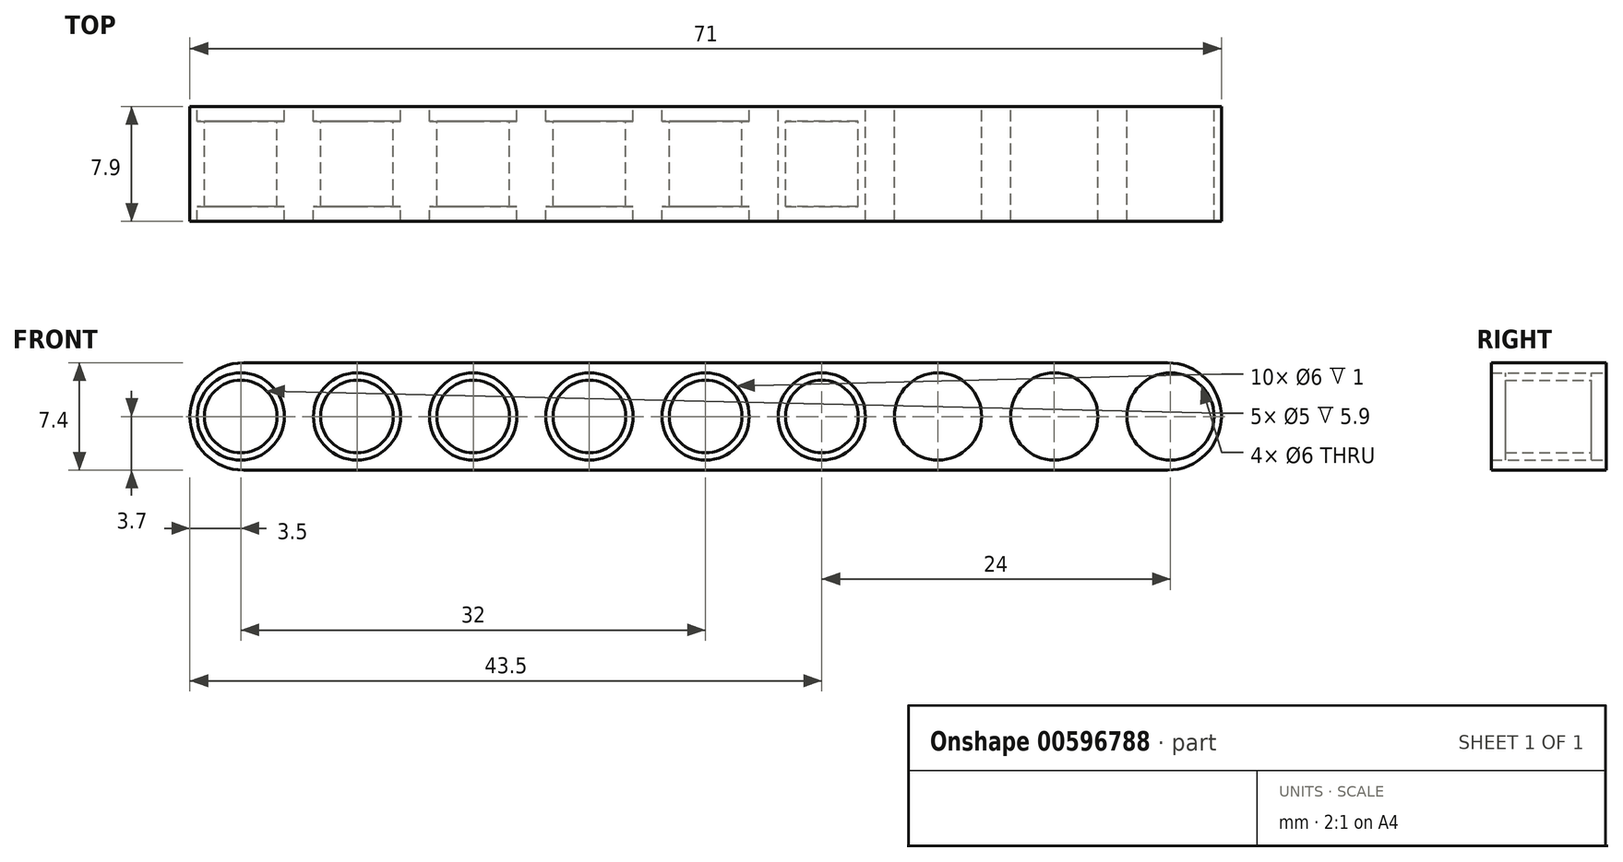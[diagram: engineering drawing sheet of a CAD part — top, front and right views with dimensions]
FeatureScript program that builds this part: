
annotation { "Feature Type Name" : "Feature", "Feature Type Description" : "" }
export const myFeature = defineFeature(function(context is Context, id is Id, definition is map)
    precondition{}
    {
        {
            var Q0;
            Q0=qCreatedBy(makeId("Front.planeOp"),FACE);
            var sketch = newSketch(context, id + "F0", { "sketchPlane" : qUnion([Q0])});
            skLineSegment(sketch, "E0.bottom", {"start": v(35.5, 3.7) * mm, "end": v(-35.5, 3.7) * mm});
            skLineSegment(sketch, "E0.top", {"start": v(35.5, -3.7) * mm, "end": v(-35.5, -3.7) * mm});
            skLineSegment(sketch, "E0.left", {"start": v(35.5, 3.7) * mm, "end": v(35.5, -3.7) * mm});
            skLineSegment(sketch, "E0.right", {"start": v(-35.5, 3.7) * mm, "end": v(-35.5, -3.7) * mm});
            skPoint(sketch, "E0.middle", {"position": v(0, 0) * mm});
            skCircle(sketch, "E1", {"center": v(0, 0) * mm, "radius": 2.5 * mm});
            skCircle(sketch, "E2", {"center": v(-8, 0) * mm, "radius": 2.5 * mm});
            skCircle(sketch, "E3", {"center": v(-16, 0) * mm, "radius": 2.5 * mm});
            skCircle(sketch, "E4", {"center": v(-24, 0) * mm, "radius": 2.5 * mm});
            skCircle(sketch, "E5", {"center": v(-32, 0) * mm, "radius": 2.5 * mm});
            skCircle(sketch, "E6", {"center": v(0, 0) * mm, "radius": 3 * mm});
            skCircle(sketch, "E7", {"center": v(-8, 0) * mm, "radius": 3 * mm});
            skCircle(sketch, "E8", {"center": v(-16, 0) * mm, "radius": 3 * mm});
            skCircle(sketch, "E9", {"center": v(-24, 0) * mm, "radius": 3 * mm});
            skCircle(sketch, "E10", {"center": v(-32, 0) * mm, "radius": 3 * mm});
            skLineSegment(sketch, "E11", {"start": v(0, 8.17) * mm, "end": v(0, -9.62) * mm, "construction": true});
            skPoint(sketch, "E11.endSnap0", {"position": v(0, -3.7) * mm});
            skCircle(sketch, "E12.MirrorC", {"center": v(8, 0) * mm, "radius": 2.5 * mm});
            skCircle(sketch, "E13.MirrorC", {"center": v(8, 0) * mm, "radius": 3 * mm});
            skCircle(sketch, "E14.MirrorC", {"center": v(16, 0) * mm, "radius": 3 * mm});
            skCircle(sketch, "E15.MirrorC", {"center": v(16, 0) * mm, "radius": 2.5 * mm});
            skCircle(sketch, "E16.MirrorC", {"center": v(24, 0) * mm, "radius": 3 * mm});
            skCircle(sketch, "E17.MirrorC", {"center": v(24, 0) * mm, "radius": 2.5 * mm});
            skCircle(sketch, "E18.MirrorC", {"center": v(32, 0) * mm, "radius": 3 * mm});
            skCircle(sketch, "E19.MirrorC", {"center": v(32, 0) * mm, "radius": 2.5 * mm});
            skSolve(sketch);
        }
        {
            var Q0;
            Q0=makeQuery(id+"F0.imprint","IMPRINT",FACE,{"disambiguationData":[TD([[makeQuery(id+"F0.imprint","IMPRINT",EDGE,{"derivedFrom":sQuery(id+"F0.wireOp",EDGE,"E0.bottom")}),1.0]])]});
            extrude(context, id + "F1", {"entities" : qUnion([Q0]), "endBound" : BoundingType.SYMMETRIC, "depth" : 7.9 * mm, "offsetDistance" : 25 * mm});
        }
        {
            var Q0;
            Q0=makeQuery(id+"F0.imprint","IMPRINT",FACE,{"disambiguationData":[TD([[makeQuery(id+"F0.imprint","IMPRINT",EDGE,{"derivedFrom":sQuery(id+"F0.wireOp",EDGE,"E5")}),-1.0]])]});
            var Q1;
            Q1=makeQuery(id+"F0.imprint","IMPRINT",FACE,{"disambiguationData":[TD([[makeQuery(id+"F0.imprint","IMPRINT",EDGE,{"derivedFrom":sQuery(id+"F0.wireOp",EDGE,"E4")}),-1.0]])]});
            var Q2;
            Q2=makeQuery(id+"F0.imprint","IMPRINT",FACE,{"disambiguationData":[TD([[makeQuery(id+"F0.imprint","IMPRINT",EDGE,{"derivedFrom":sQuery(id+"F0.wireOp",EDGE,"E3")}),-1.0]])]});
            var Q3;
            Q3=makeQuery(id+"F0.imprint","IMPRINT",FACE,{"disambiguationData":[TD([[makeQuery(id+"F0.imprint","IMPRINT",EDGE,{"derivedFrom":sQuery(id+"F0.wireOp",EDGE,"E2")}),-1.0]])]});
            var Q4;
            Q4=makeQuery(id+"F0.imprint","IMPRINT",FACE,{"disambiguationData":[TD([[makeQuery(id+"F0.imprint","IMPRINT",EDGE,{"derivedFrom":sQuery(id+"F0.wireOp",EDGE,"E1")}),-1.0]])]});
            var Q5;
            Q5=makeQuery(id+"F0.imprint","IMPRINT",FACE,{"disambiguationData":[TD([[makeQuery(id+"F0.imprint","IMPRINT",EDGE,{"derivedFrom":sQuery(id+"F0.wireOp",EDGE,"E12.MirrorC")}),1.0]])]});
            var Q6;
            Q6=makeQuery(id+"F0.imprint","IMPRINT",FACE,{"disambiguationData":[TD([[makeQuery(id+"F0.imprint","IMPRINT",EDGE,{"derivedFrom":sQuery(id+"F0.wireOp",EDGE,"E14.MirrorC")}),-1.0]])]});
            var Q7;
            Q7=makeQuery(id+"F0.imprint","IMPRINT",FACE,{"disambiguationData":[TD([[makeQuery(id+"F0.imprint","IMPRINT",EDGE,{"derivedFrom":sQuery(id+"F0.wireOp",EDGE,"E16.MirrorC")}),-1.0]])]});
            var Q8;
            Q8=makeQuery(id+"F0.imprint","IMPRINT",FACE,{"disambiguationData":[TD([[makeQuery(id+"F0.imprint","IMPRINT",EDGE,{"derivedFrom":sQuery(id+"F0.wireOp",EDGE,"E18.MirrorC")}),-1.0]])]});
            extrude(context, id + "F2", {"entities" : qUnion([Q0, Q1, Q2, Q3, Q4, Q5, Q6, Q7, Q8]), "operationType" : NewBodyOperationType.ADD, "endBound" : BoundingType.SYMMETRIC, "depth" : 5.9 * mm, "offsetDistance" : 25 * mm});
        }
        {
            var Q0;
            Q0=makeQuery(id+"F1.opExtrude","SWEPT_EDGE",EDGE,{"disambiguationData":[OSD([sQuery(id+"F0.wireOp",EDGE,"E0.bottom"),sQuery(id+"F0.wireOp",EDGE,"E0.right")])]});
            var Q1;
            Q1=makeQuery(id+"F1.opExtrude","SWEPT_EDGE",EDGE,{"disambiguationData":[OSD([sQuery(id+"F0.wireOp",EDGE,"E0.top"),sQuery(id+"F0.wireOp",EDGE,"E0.right")])]});
            var Q2;
            Q2=makeQuery(id+"F1.opExtrude","SWEPT_EDGE",EDGE,{"disambiguationData":[OSD([sQuery(id+"F0.wireOp",EDGE,"E0.bottom"),sQuery(id+"F0.wireOp",EDGE,"E0.left")])]});
            var Q3;
            Q3=makeQuery(id+"F1.opExtrude","SWEPT_EDGE",EDGE,{"disambiguationData":[OSD([sQuery(id+"F0.wireOp",EDGE,"E0.top"),sQuery(id+"F0.wireOp",EDGE,"E0.left")])]});
            fillet(context, id + "F3", {"entities" : qUnion([Q0, Q1, Q2, Q3]), "radius" : 3.7 * mm, "tangentPropagation" : true, "allowEdgeOverflow" : false});
        }
    });
